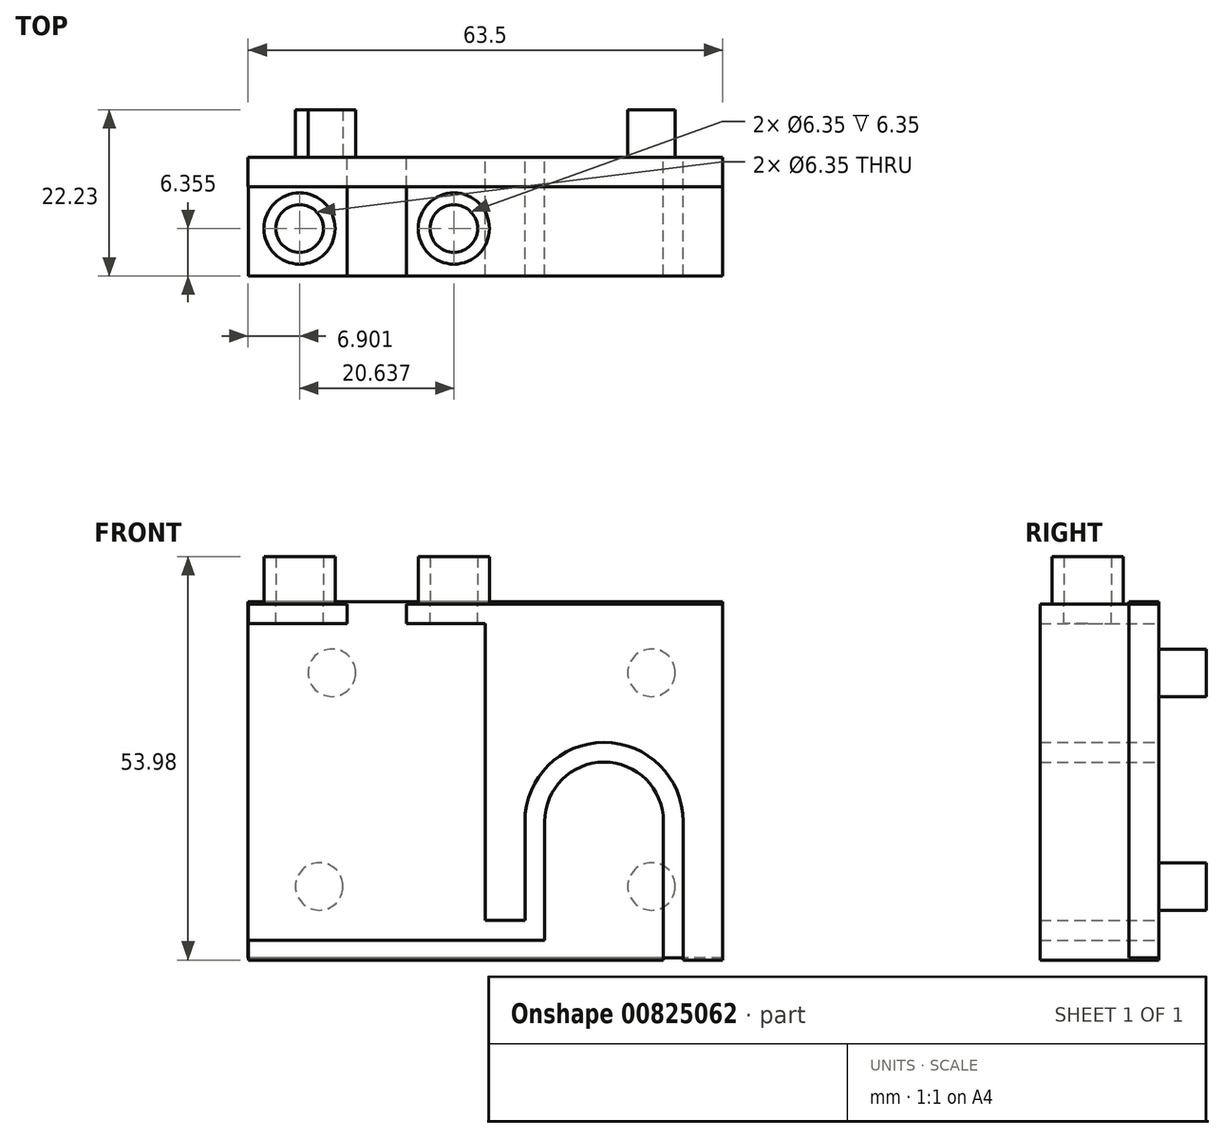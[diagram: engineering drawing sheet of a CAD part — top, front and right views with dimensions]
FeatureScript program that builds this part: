
annotation { "Feature Type Name" : "Feature", "Feature Type Description" : "" }
export const myFeature = defineFeature(function(context is Context, id is Id, definition is map)
    precondition{}
    {
        {
            var Q0;
            Q0=qCreatedBy(makeId("Front.planeOp"),FACE);
            var sketch = newSketch(context, id + "F0", { "sketchPlane" : qUnion([Q0])});
            skLineSegment(sketch, "E0.bottom", {"start": v(-31.75, 44.98) * mm, "end": v(0, 44.98) * mm});
            skLineSegment(sketch, "E0.top", {"start": v(-31.75, 0) * mm, "end": v(0, 0) * mm});
            skLineSegment(sketch, "E0.left", {"start": v(-31.75, 44.98) * mm, "end": v(-31.75, 0) * mm});
            skLineSegment(sketch, "E0.right", {"start": v(0, 44.98) * mm, "end": v(0, 0) * mm});
            skLineSegment(sketch, "E1.bottom", {"start": v(-26.46, 0) * mm, "end": v(-23.81, 0) * mm});
            skLineSegment(sketch, "E1.top", {"start": v(-26.46, 15.88) * mm, "end": v(-23.81, 15.88) * mm});
            skLineSegment(sketch, "E1.left", {"start": v(-26.46, 0) * mm, "end": v(-26.46, 15.87) * mm});
            skLineSegment(sketch, "E1.right", {"start": v(-23.81, 0) * mm, "end": v(-23.81, 15.87) * mm});
            skLineSegment(sketch, "E2.bottom", {"start": v(-7.94, 0) * mm, "end": v(-5.3, 0) * mm});
            skLineSegment(sketch, "E2.top", {"start": v(-7.94, 15.88) * mm, "end": v(-5.3, 15.88) * mm});
            skLineSegment(sketch, "E2.left", {"start": v(-7.94, 0) * mm, "end": v(-7.94, 15.87) * mm});
            skLineSegment(sketch, "E2.right", {"start": v(-5.3, 0) * mm, "end": v(-5.3, 15.87) * mm});
            skArc(sketch, "E3", {"start": v(-5.3, 15.87) * mm, "mid": v(-15.87, 26.46) * mm, "end": v(-26.46, 15.88) * mm});
            skArc(sketch, "E4", {"start": v(-7.94, 15.87) * mm, "mid": v(-15.87, 23.81) * mm, "end": v(-23.81, 15.87) * mm});
            skLineSegment(sketch, "E5.bottom", {"start": v(-26.46, 0) * mm, "end": v(-31.75, 0) * mm});
            skLineSegment(sketch, "E5.top", {"start": v(-26.46, 2.65) * mm, "end": v(-31.75, 2.65) * mm});
            skLineSegment(sketch, "E5.left", {"start": v(-26.46, 0) * mm, "end": v(-26.46, 2.65) * mm});
            skLineSegment(sketch, "E5.right", {"start": v(-31.75, 0) * mm, "end": v(-31.75, 2.65) * mm});
            skLineSegment(sketch, "E6.bottom", {"start": v(-31.75, 44.98) * mm, "end": v(-63.47, 44.98) * mm});
            skLineSegment(sketch, "E6.top", {"start": v(-31.75, 42.34) * mm, "end": v(-63.47, 42.34) * mm});
            skLineSegment(sketch, "E6.left", {"start": v(-31.75, 44.98) * mm, "end": v(-31.75, 42.34) * mm});
            skLineSegment(sketch, "E6.right", {"start": v(-63.47, 44.98) * mm, "end": v(-63.47, 42.34) * mm});
            skLineSegment(sketch, "E7.bottom", {"start": v(-63.47, 42.34) * mm, "end": v(-60.82, 42.34) * mm});
            skLineSegment(sketch, "E7.top", {"start": v(-63.47, 0) * mm, "end": v(-60.82, 0) * mm});
            skLineSegment(sketch, "E7.left", {"start": v(-63.47, 42.34) * mm, "end": v(-63.47, 0) * mm});
            skLineSegment(sketch, "E7.right", {"start": v(-60.82, 42.34) * mm, "end": v(-60.82, 0) * mm});
            skLineSegment(sketch, "E8.bottom", {"start": v(-63.47, 0) * mm, "end": v(0, 0) * mm});
            skLineSegment(sketch, "E8.top", {"start": v(-63.47, -2.65) * mm, "end": v(0, -2.65) * mm});
            skLineSegment(sketch, "E8.left", {"start": v(-63.47, 0) * mm, "end": v(-63.47, -2.65) * mm});
            skLineSegment(sketch, "E8.right", {"start": v(0, 0) * mm, "end": v(0, -2.65) * mm});
            skLineSegment(sketch, "E9.top", {"start": v(-7.94, -2.65) * mm, "end": v(-5.3, -2.65) * mm});
            skLineSegment(sketch, "E9.left", {"start": v(-7.94, 0) * mm, "end": v(-7.94, -2.65) * mm});
            skLineSegment(sketch, "E9.right", {"start": v(-5.3, 0) * mm, "end": v(-5.3, -2.65) * mm});
            skLineSegment(sketch, "E10.bottom", {"start": v(-58.18, 44.98) * mm, "end": v(-55.53, 44.98) * mm});
            skLineSegment(sketch, "E10.top", {"start": v(-58.18, 42.34) * mm, "end": v(-55.53, 42.34) * mm});
            skLineSegment(sketch, "E11.bottom", {"start": v(-50.25, 44.98) * mm, "end": v(-42.31, 44.98) * mm});
            skLineSegment(sketch, "E11.top", {"start": v(-50.25, 42.34) * mm, "end": v(-42.31, 42.34) * mm});
            skLineSegment(sketch, "E11.left", {"start": v(-50.25, 44.98) * mm, "end": v(-50.25, 42.34) * mm});
            skLineSegment(sketch, "E11.right", {"start": v(-42.31, 44.98) * mm, "end": v(-42.31, 42.34) * mm});
            skLineSegment(sketch, "E12.bottom", {"start": v(-37.04, 44.98) * mm, "end": v(-34.4, 44.98) * mm});
            skLineSegment(sketch, "E12.top", {"start": v(-37.04, 42.34) * mm, "end": v(-34.4, 42.34) * mm});
            skSolve(sketch);
        }
        {
            var Q0;
            Q0=makeQuery(id+"F0.imprint","IMPRINT",FACE,{"disambiguationData":[TD([[makeQuery(id+"F0.imprint","IMPRINT",EDGE,{"derivedFrom":sQuery(id+"F0.wireOp",EDGE,"E0.bottom")}),-1.0]])]});
            var Q1;
            {var subQ0=sQuery(id+"F0.wireOp",EDGE,"E1.right");Q1=makeQuery(id+"F0.imprint","IMPRINT",FACE,{"disambiguationData":[TD([[makeQuery(id+"F0.imprint","IMPRINT",EDGE,{"derivedFrom":subQ0}),-1.0]])]});}
            var Q2;
            {var subQ6=sQuery(id+"F0.wireOp",EDGE,"E8.left");Q2=makeQuery(id+"F0.imprint","IMPRINT",FACE,{"disambiguationData":[TD([[makeQuery(id+"F0.imprint","IMPRINT",EDGE,{"derivedFrom":subQ6}),1.0]])]});}
            var Q3;
            {var subQ0=sQuery(id+"F0.wireOp",EDGE,"E8.right");Q3=makeQuery(id+"F0.imprint","IMPRINT",FACE,{"disambiguationData":[TD([[makeQuery(id+"F0.imprint","IMPRINT",EDGE,{"derivedFrom":subQ0}),-1.0]])]});}
            var Q4;
            Q4=makeQuery(id+"F0.imprint","IMPRINT",FACE,{"disambiguationData":[TD([[makeQuery(id+"F0.imprint","IMPRINT",EDGE,{"derivedFrom":sQuery(id+"F0.wireOp",EDGE,"E7.bottom")}),-1.0]])]});
            var Q5;
            {var subQ1=sQuery(id+"F0.wireOp",EDGE,"E6.right");Q5=makeQuery(id+"F0.imprint","IMPRINT",FACE,{"disambiguationData":[TD([[makeQuery(id+"F0.imprint","IMPRINT",EDGE,{"derivedFrom":subQ1}),1.0]])]});}
            var Q6;
            {var subQ0=sQuery(id+"F0.wireOp",EDGE,"E10.right");Q6=makeQuery(id+"F0.imprint","IMPRINT",FACE,{"disambiguationData":[TD([[makeQuery(id+"F0.imprint","IMPRINT",EDGE,{"derivedFrom":subQ0}),1.0]])]});}
            var Q7;
            {var subQ0=sQuery(id+"F0.wireOp",EDGE,"E11.right");Q7=makeQuery(id+"F0.imprint","IMPRINT",FACE,{"disambiguationData":[TD([[makeQuery(id+"F0.imprint","IMPRINT",EDGE,{"derivedFrom":subQ0}),1.0]])]});}
            var Q8;
            {var subQ0=sQuery(id+"F0.wireOp",EDGE,"E6.left");Q8=makeQuery(id+"F0.imprint","IMPRINT",FACE,{"disambiguationData":[TD([[makeQuery(id+"F0.imprint","IMPRINT",EDGE,{"derivedFrom":subQ0}),-1.0]])]});}
            extrude(context, id + "F1", {"entities" : qUnion([Q0, Q1, Q2, Q3, Q4, Q5, Q6, Q7, Q8]), "depth" : 15.88 * mm, "offsetDistance" : 25.4 * mm});
        }
        {
            var Q0;
            Q0=qCreatedBy(makeId("Front.planeOp"),FACE);
            var sketch = newSketch(context, id + "F2", { "sketchPlane" : qUnion([Q0])});
            skLineSegment(sketch, "E13.bottom", {"start": v(0, 45.3) * mm, "end": v(-63.5, 45.3) * mm});
            skLineSegment(sketch, "E13.top", {"start": v(0, -2.33) * mm, "end": v(-63.5, -2.33) * mm});
            skLineSegment(sketch, "E13.left", {"start": v(0, 45.3) * mm, "end": v(0, -2.33) * mm});
            skLineSegment(sketch, "E13.right", {"start": v(-63.5, 45.3) * mm, "end": v(-63.5, -2.33) * mm});
            skCircle(sketch, "E14", {"center": v(-9.53, 35.77) * mm, "radius": 3.18 * mm});
            skCircle(sketch, "E15", {"center": v(-52.28, 35.77) * mm, "radius": 3.18 * mm});
            skCircle(sketch, "E16", {"center": v(-53.97, 7.2) * mm, "radius": 3.18 * mm});
            skCircle(sketch, "E17", {"center": v(-9.52, 7.2) * mm, "radius": 3.18 * mm});
            skSolve(sketch);
        }
        {
            var Q0;
            Q0=qSketchRegion(id+"F2",true);
            var Q1;
            Q1=makeQuery(id+"F2.imprint","IMPRINT",FACE,{"disambiguationData":[TD([[makeQuery(id+"F2.imprint","IMPRINT",EDGE,{"derivedFrom":sQuery(id+"F2.wireOp",EDGE,"E15")}),1.0]])]});
            var Q2;
            Q2=makeQuery(id+"F2.imprint","IMPRINT",FACE,{"disambiguationData":[TD([[makeQuery(id+"F2.imprint","IMPRINT",EDGE,{"derivedFrom":sQuery(id+"F2.wireOp",EDGE,"E16")}),1.0]])]});
            var Q3;
            Q3=makeQuery(id+"F2.imprint","IMPRINT",FACE,{"disambiguationData":[TD([[makeQuery(id+"F2.imprint","IMPRINT",EDGE,{"derivedFrom":sQuery(id+"F2.wireOp",EDGE,"E17")}),1.0]])]});
            var Q4;
            Q4=makeQuery(id+"F2.imprint","IMPRINT",FACE,{"disambiguationData":[TD([[makeQuery(id+"F2.imprint","IMPRINT",EDGE,{"derivedFrom":sQuery(id+"F2.wireOp",EDGE,"E14")}),1.0]])]});
            extrude(context, id + "F3", {"entities" : qUnion([Q0, Q1, Q2, Q3, Q4]), "depth" : 3.97 * mm, "offsetDistance" : 25.4 * mm});
        }
        {
            var Q0;
            Q0=makeQuery(id+"F2.imprint","IMPRINT",FACE,{"disambiguationData":[TD([[makeQuery(id+"F2.imprint","IMPRINT",EDGE,{"derivedFrom":sQuery(id+"F2.wireOp",EDGE,"E14")}),1.0]])]});
            var Q1;
            Q1=makeQuery(id+"F2.imprint","IMPRINT",FACE,{"disambiguationData":[TD([[makeQuery(id+"F2.imprint","IMPRINT",EDGE,{"derivedFrom":sQuery(id+"F2.wireOp",EDGE,"E15")}),1.0]])]});
            var Q2;
            Q2=makeQuery(id+"F2.imprint","IMPRINT",FACE,{"disambiguationData":[TD([[makeQuery(id+"F2.imprint","IMPRINT",EDGE,{"derivedFrom":sQuery(id+"F2.wireOp",EDGE,"E17")}),1.0]])]});
            var Q3;
            Q3=makeQuery(id+"F2.imprint","IMPRINT",FACE,{"disambiguationData":[TD([[makeQuery(id+"F2.imprint","IMPRINT",EDGE,{"derivedFrom":sQuery(id+"F2.wireOp",EDGE,"E16")}),1.0]])]});
            var Q4;
            Q4=sQuery(id+"F2.wireOp",EDGE,"E14");
            var Q5;
            Q5=sQuery(id+"F2.wireOp",EDGE,"E15");
            var Q6;
            Q6=sQuery(id+"F2.wireOp",EDGE,"E17");
            var Q7;
            Q7=sQuery(id+"F2.wireOp",EDGE,"E16");
            extrude(context, id + "F4", {"entities" : qUnion([Q0, Q1, Q2, Q3]), "surfaceEntities" : qUnion([Q4, Q5, Q6, Q7]), "oppositeDirection" : true, "depth" : 6.35 * mm, "offsetDistance" : 25.4 * mm});
        }
        {
            var Q0;
            Q0=makeQuery(id+"F1.opExtrude","SWEPT_FACE",FACE,{"disambiguationData":[OSD([sQuery(id+"F0.wireOp",EDGE,"E6.bottom"),sQuery(id+"F0.wireOp",EDGE,"E10.bottom")])]});
            var sketch = newSketch(context, id + "F5", { "sketchPlane" : qUnion([Q0])});
            skCircle(sketch, "E18", {"center": v(-56.6, -9.52) * mm, "radius": 3.18 * mm});
            skCircle(sketch, "E19", {"center": v(-35.96, -9.52) * mm, "radius": 3.18 * mm});
            skCircle(sketch, "E20", {"center": v(-56.6, -9.52) * mm, "radius": 4.76 * mm});
            skCircle(sketch, "E21", {"center": v(-35.96, -9.52) * mm, "radius": 4.76 * mm});
            skSolve(sketch);
        }
        {
            var Q0;
            Q0=qSketchRegion(id+"F5",true);
            extrude(context, id + "F6", {"entities" : qUnion([Q0]), "depth" : 6.35 * mm, "offsetDistance" : 25.4 * mm});
        }
        {
            var Q0;
            Q0=makeQuery(id+"F1.opExtrude","SWEPT_FACE",FACE,{"disambiguationData":[OSD([sQuery(id+"F0.wireOp",EDGE,"E6.bottom"),sQuery(id+"F0.wireOp",EDGE,"E10.bottom")])]});
            var sketch = newSketch(context, id + "F7", { "sketchPlane" : qUnion([Q0])});
            skCircle(sketch, "E22", {"center": v(-35.96, -9.52) * mm, "radius": 3.18 * mm});
            skCircle(sketch, "E23", {"center": v(-56.6, -9.52) * mm, "radius": 3.18 * mm});
            skSolve(sketch);
        }
        {
            var Q0;
            Q0=qSketchRegion(id+"F7",true);
            extrude(context, id + "F8", {"entities" : qUnion([Q0]), "operationType" : NewBodyOperationType.REMOVE, "oppositeDirection" : true, "depth" : 25.4 * mm, "offsetDistance" : 25.4 * mm});
        }
    });
